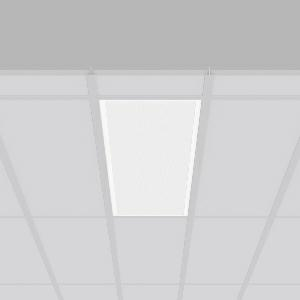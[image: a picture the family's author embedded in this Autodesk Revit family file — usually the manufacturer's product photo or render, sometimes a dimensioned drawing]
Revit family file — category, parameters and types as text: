
# Revit family: sidelite_eco_672368_002_f187
name_source: partatom
category: Lighting Fixtures
units: mm (PartAtom-declared; Revit-internal decimal feet)

## family parameters
Cut with Voids When Loaded = No
Host = Face
Light Source = No
Part Type = Normal
Room Calculation Point = No
Round Connector Dimension = Use Diameter
Shared = No

## types (1)
- SIDELITE ECO (1 x LED Modul 830, 3200 lm, 3000)
    Apparent Load = 29 VA
    CIE Flux Codes = 59 87 97 100 100
    Color Rendering = 80
    Color Temperature = 3000
    Default Elevation = 1800 mm
    Description = Series: SIDELITE ECO
Highly economical recessed luminaire with progressive LED technology. For escape route illumination. Frame made of aluminium, powder-coated. Diffuser plastic microprismatic. Lightguide and diffuser made of non-yellowing plastic (PMMA). Lateral light emission (RZB SIDELITE technology) for homogeneous light distribution. External driver. Self-contained system with automatic self-test. External driver with simple plug-in locking system. Extended connection cable (1.90 m). 
Colour: white
Length: 1195 mm
Width: 295 mm
Cut-out length: 1170 mm
Cut-out width: 270 mm
Recess height: 160 mm
Luminaire: recess height: 40 mm
Weight: 4.4 kg
Operating mode: maintained power mode
Duration time: 3 h
Lamp: LED
Socket: without socket
Colour temperature: 3000K
Colour rendering index (CRI): 80
System power: 29 W
Rated luminous flux: 3200 lm
Luminous flux, emergency: 470 lm
System power, emergency: -
Control gear: Regulated power supply
Protection class: I
Type of protection: IP 40
    Height = 0 mm  [stored 0 ft]
    Lamp = 1 x LED Modul 830
    Lamp Light Flux = 3200 lm
    Lamp count = 1
    Length = 1195 mm
    Lifetime = 50000 h
    Luminous efficacy = 110 lm/W
    Manufacturer = RZB
    ModVariant = No
    Model = 672368.002
    Mounting Place = Ceiling
    Mounting Type = Recessed
    Number of Poles = 1
    OnlyDefault = Yes
    Power Factor = 1
    Product Name = SIDELITE ECO
    Product group = Recessed modular luminaires
    ProductGroupID = 406
    Protection Class = Protection class I
    Protection Degree = IP 40
    RLX_Detail_Level = 1
    RLX_Emergency_Light_Flux = 470 lm
    RLX_Emergency_Type = 3
    RLX_Emergency_Type_DB = Yes
    RlxData = <blob elided: 34701 chars, md5=bf782fae>
    Socket = socket
    Standby Power = 0 W
    System Light Flux = 3200 lm
    System Power = 29 W
    Type Comments = Product without accessories
    Type Image = 312366.002.jpg
    URL = http://relux.com
    VarID = ---
    Voltage = 230 V
    Voltage Range = 220-240 V
    Weight = 0.00 kg
    Width = 295 mm

note: [stored X ft] marks values corroborated as IEEE doubles in the binary element streams (Revit-internal decimal feet)

## geometry (parser evidence)
native form markers: Blend x4, Sweep x12
no freeform markers — native parametric forms only
